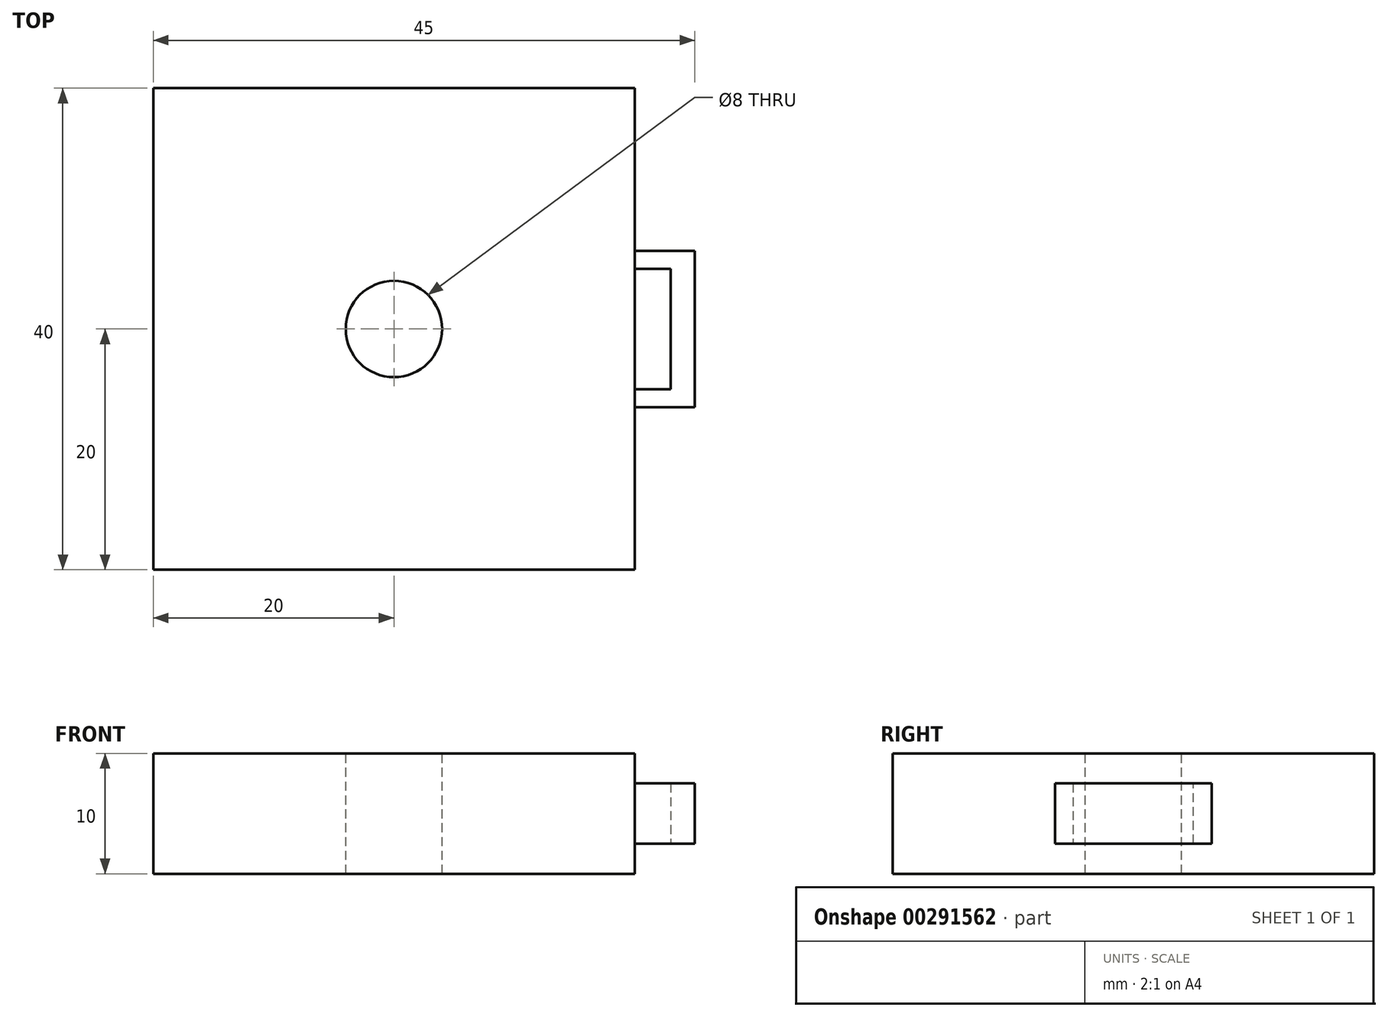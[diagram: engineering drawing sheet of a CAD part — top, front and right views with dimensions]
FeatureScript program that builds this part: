
annotation { "Feature Type Name" : "Feature", "Feature Type Description" : "" }
export const myFeature = defineFeature(function(context is Context, id is Id, definition is map)
    precondition{}
    {
        {
            var Q0;
            Q0=qCreatedBy(makeId("Top.planeOp"),FACE);
            var sketch = newSketch(context, id + "F0", { "sketchPlane" : qUnion([Q0])});
            skLineSegment(sketch, "E0.bottom", {"start": v(0, 0) * mm, "end": v(40, 0) * mm});
            skLineSegment(sketch, "E0.top", {"start": v(0, -40) * mm, "end": v(40, -40) * mm});
            skLineSegment(sketch, "E0.left", {"start": v(0, 0) * mm, "end": v(0, -40) * mm});
            skLineSegment(sketch, "E0.right", {"start": v(40, 0) * mm, "end": v(40, -40) * mm});
            skSolve(sketch);
        }
        {
            var Q0;
            Q0=makeQuery(id+"F0.imprint","IMPRINT",FACE,{"disambiguationData":[TD([[makeQuery(id+"F0.imprint","IMPRINT",EDGE,{"derivedFrom":sQuery(id+"F0.wireOp",EDGE,"E0.bottom")}),-1.0]])]});
            extrude(context, id + "F1", {"entities" : qUnion([Q0]), "depth" : 10 * mm});
        }
        {
            var Q0;
            Q0=makeQuery(id+"F1.opExtrude","CAP_FACE",FACE,{"disambiguationData":[OSD([sQuery(id+"F0.wireOp",EDGE,"E0.bottom"),sQuery(id+"F0.wireOp",EDGE,"E0.top"),sQuery(id+"F0.wireOp",EDGE,"E0.left"),sQuery(id+"F0.wireOp",EDGE,"E0.right")])],"isStart":false});
            var sketch = newSketch(context, id + "F2", { "sketchPlane" : qUnion([Q0])});
            skCircle(sketch, "E1", {"center": v(20, -20) * mm, "radius": 4 * mm});
            skPoint(sketch, "E1.centerSnap0", {"position": v(20, 0) * mm});
            skPoint(sketch, "E1.centerSnap1", {"position": v(0, -20) * mm});
            skSolve(sketch);
        }
        {
            var Q0;
            Q0 = qSketchRegion(id + "F2", true);
            extrude(context, id + "F3", {"entities" : qUnion([Q0]), "operationType" : NewBodyOperationType.REMOVE, "endBound" : BoundingType.THROUGH_ALL, "oppositeDirection" : true, "depth" : 25 * mm});
        }
        {
            var Q0;
            Q0=makeQuery(id+"F1.opExtrude","SWEPT_FACE",FACE,{"disambiguationData":[OSD([sQuery(id+"F0.wireOp",EDGE,"E0.right")])]});
            var sketch = newSketch(context, id + "F4", { "sketchPlane" : qUnion([Q0])});
            skLineSegment(sketch, "E2.bottom", {"start": v(-26.5, 7.5) * mm, "end": v(-25, 7.5) * mm});
            skLineSegment(sketch, "E2.top", {"start": v(-26.5, 2.5) * mm, "end": v(-25, 2.5) * mm});
            skLineSegment(sketch, "E2.left", {"start": v(-26.5, 7.5) * mm, "end": v(-26.5, 2.5) * mm});
            skLineSegment(sketch, "E2.right", {"start": v(-25, 7.5) * mm, "end": v(-25, 2.5) * mm});
            skLineSegment(sketch, "E3", {"start": v(-20, 10) * mm, "end": v(-20, 0) * mm, "construction": true});
            skLineSegment(sketch, "E4", {"start": v(-40, 5) * mm, "end": v(0, 5) * mm, "construction": true});
            skLineSegment(sketch, "E5.MirrorCS", {"start": v(-25, 2.5) * mm, "end": v(-25, 7.5) * mm});
            skLineSegment(sketch, "E6.MirrorCS", {"start": v(-26.5, 2.5) * mm, "end": v(-26.5, 7.5) * mm});
            skLineSegment(sketch, "E7.MirrorCS", {"start": v(-20, 0) * mm, "end": v(-20, 10) * mm, "construction": true});
            skLineSegment(sketch, "E8.MirrorCS", {"start": v(-13.5, 2.5) * mm, "end": v(-15, 2.5) * mm});
            skLineSegment(sketch, "E9.MirrorCS", {"start": v(-13.5, 2.5) * mm, "end": v(-13.5, 7.5) * mm});
            skLineSegment(sketch, "E10.MirrorCS", {"start": v(-15, 2.5) * mm, "end": v(-15, 7.5) * mm});
            skLineSegment(sketch, "E11.MirrorCS", {"start": v(-13.5, 7.5) * mm, "end": v(-15, 7.5) * mm});
            skLineSegment(sketch, "E12.MirrorCS", {"start": v(-15, 7.5) * mm, "end": v(-15, 2.5) * mm});
            skLineSegment(sketch, "E13.MirrorCS", {"start": v(-13.5, 7.5) * mm, "end": v(-13.5, 2.5) * mm});
            skLineSegment(sketch, "E14.MirrorCS", {"start": v(0, 5) * mm, "end": v(-40, 5) * mm, "construction": true});
            skSolve(sketch);
        }
        {
            var Q0;
            Q0=makeQuery(id+"F4.imprint","IMPRINT",FACE,{"disambiguationData":[TD([[makeQuery(id+"F4.imprint","IMPRINT",EDGE,{"derivedFrom":sQuery(id+"F4.wireOp",EDGE,"E2.top")}),1.0]])]});
            var Q1;
            Q1=makeQuery(id+"F4.imprint","IMPRINT",FACE,{"disambiguationData":[TD([[makeQuery(id+"F4.imprint","IMPRINT",EDGE,{"derivedFrom":sQuery(id+"F4.wireOp",EDGE,"E11.MirrorCS")}),1.0]])]});
            extrude(context, id + "F5", {"entities" : qUnion([Q0, Q1]), "operationType" : NewBodyOperationType.ADD, "depth" : 3 * mm});
        }
        {
            var Q0;
            Q0=makeQuery(id+"F5.opExtrude","CAP_FACE",FACE,{"disambiguationData":[OSD([sQuery(id+"F4.wireOp",EDGE,"E2.top"),sQuery(id+"F4.wireOp",EDGE,"E6.MirrorCS"),sQuery(id+"F4.wireOp",EDGE,"E2.bottom"),sQuery(id+"F4.wireOp",EDGE,"E5.MirrorCS")])],"isStart":false});
            var sketch = newSketch(context, id + "F6", { "sketchPlane" : qUnion([Q0])});
            skLineSegment(sketch, "E15.bottom", {"start": v(-26.5, 7.5) * mm, "end": v(-13.5, 7.5) * mm});
            skLineSegment(sketch, "E15.top", {"start": v(-26.5, 2.5) * mm, "end": v(-13.5, 2.5) * mm});
            skLineSegment(sketch, "E15.left", {"start": v(-26.5, 7.5) * mm, "end": v(-26.5, 2.5) * mm});
            skLineSegment(sketch, "E15.right", {"start": v(-13.5, 7.5) * mm, "end": v(-13.5, 2.5) * mm});
            skSolve(sketch);
        }
        {
            var Q0;
            Q0 = qSketchRegion(id + "F6", true);
            extrude(context, id + "F7", {"entities" : qUnion([Q0]), "operationType" : NewBodyOperationType.ADD, "depth" : 2 * mm});
        }
    });
